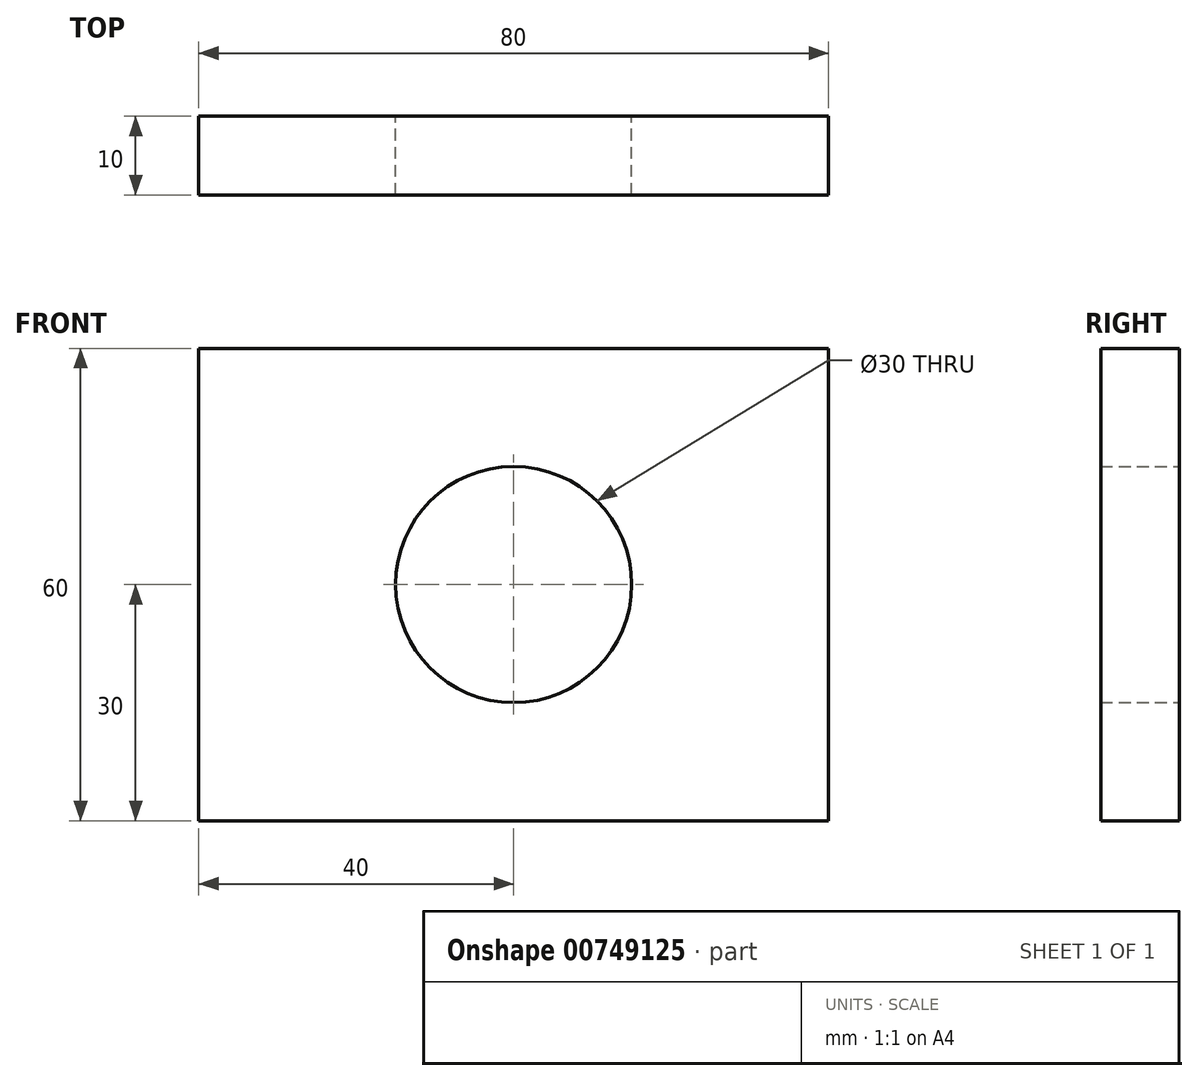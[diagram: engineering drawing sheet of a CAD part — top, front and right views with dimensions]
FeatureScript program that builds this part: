
annotation { "Feature Type Name" : "Feature", "Feature Type Description" : "" }
export const myFeature = defineFeature(function(context is Context, id is Id, definition is map)
    precondition{}
    {
        {
            var Q0;
            Q0=qCreatedBy(makeId("Front.planeOp"),FACE);
            var sketch = newSketch(context, id + "F0", { "sketchPlane" : qUnion([Q0])});
            skLineSegment(sketch, "E0", {"start": v(0, 0) * mm, "end": v(80, 0) * mm});
            skLineSegment(sketch, "E1", {"start": v(80, 0) * mm, "end": v(80, 60) * mm});
            skLineSegment(sketch, "E2", {"start": v(80, 60) * mm, "end": v(0, 60) * mm});
            skLineSegment(sketch, "E3", {"start": v(0, 60) * mm, "end": v(0, 0) * mm});
            skCircle(sketch, "E4", {"center": v(40, 30) * mm, "radius": 15 * mm});
            skSolve(sketch);
        }
        {
            var Q0;
            Q0=makeQuery(id+"F0.imprint","IMPRINT",FACE,{"disambiguationData":[TD([[makeQuery(id+"F0.imprint","IMPRINT",EDGE,{"derivedFrom":sQuery(id+"F0.wireOp",EDGE,"E0")}),1.0]])]});
            extrude(context, id + "F1", {"entities" : qUnion([Q0]), "depth" : 10 * mm, "offsetDistance" : 25 * mm});
        }
    });
